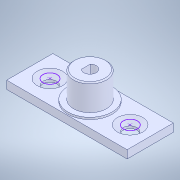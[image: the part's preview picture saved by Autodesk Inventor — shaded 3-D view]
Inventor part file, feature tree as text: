
AUTODESK INVENTOR PART (.ipt)
format: ipt  version: 2021 (Build 250183000, 183)  size: 164,864 bytes
history: mixed  units: in
note: dims shown in document units (in); Inventor stores cm internally (conversion verified against a paired STEP export)
features: sketch x5, extrude x4, chamfer x2, projected_geometry x2, hole x1, other x1, imported_body x1
ambient origin geometry x8: Origin, YZ Plane, XZ Plane, XY Plane, X Axis, Y Axis, Z Axis, Center Point
bodies: Solid1 (imported_parasolid)
feature tree (16):
  extrude  "Extrusion1"  Depth=0.3937in TaperAngle=0.0deg
  extrude  "Extrusion2"  Depth=0.3937in TaperAngle=0.0deg
  extrude  "Extrusion3"  Depth=0.0787in
  extrude  "Extrusion4"  Depth=0.0787in TaperAngle=45.0deg
  chamfer  "Chamfer1"  Distance=0.0039in
  hole  "Hole2"  [1 undecoded]
  chamfer  "Chamfer2"  [1 undecoded]
  sketch  "Sketch1"  dims[d1=0.3937in d2=0.0in d3=0.3937in d4=0.0in]
  projected_geometry  "Projected Loop1"
  sketch  "Sketch2"  dims[d5=0.0039in d6=0.3937in d7=0.0in]
  sketch  "Sketch3"  dims[d8=0.0118in d9=0.0787in d10=45.0deg]
  sketch  "Sketch6"  dims[d19=0.1339in d20=0.2362in d21=0.248in d22=0.0787in d23=90.0deg d24=0.315in d25=0.0in d26=0.002in]
  sketch  "Sketch7"  dims[d27=0.002in d28=0.0079in d29=0.0787in d30=45.0deg d31=0.0039in d32=0.3937in d33=0.0in]
  projected_geometry  "Projected Loop2"
  other  "CSK for M4 Countersunk Flat Head Screw1"
  imported_body  NMx_Import_Brep_tag  [imported B-rep: ~18 faces, bbox_mm=[30.0, 9.0, 11.5]]
note: 2 required parameter values undecoded (feature->parameter linkage not recoverable at this tier; creation-order binding heuristic only, values carry confidence <= 0.55)
